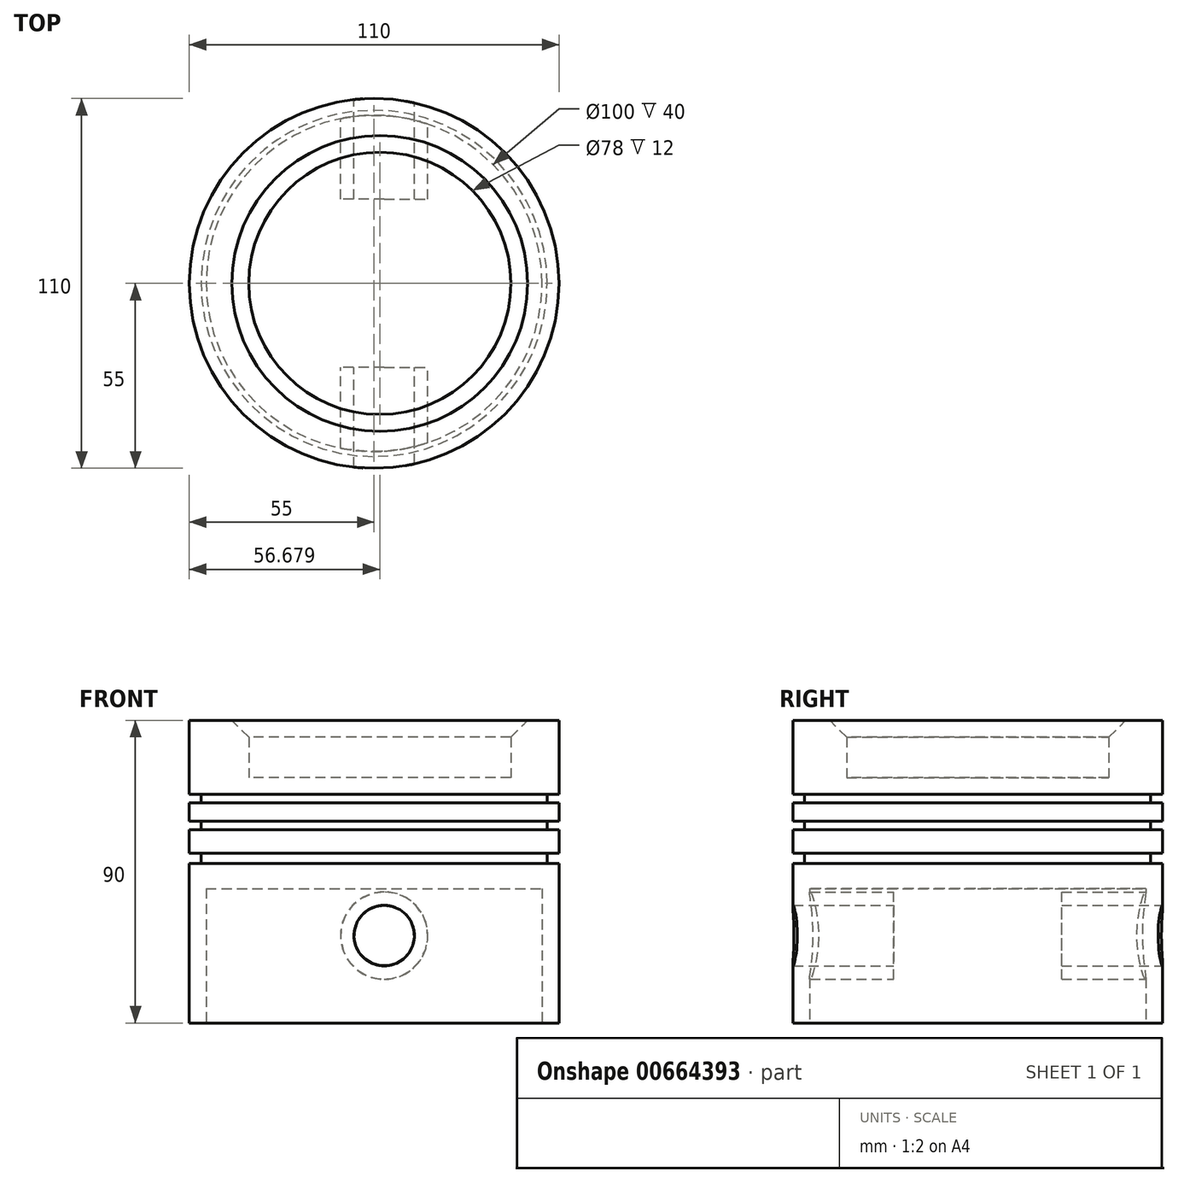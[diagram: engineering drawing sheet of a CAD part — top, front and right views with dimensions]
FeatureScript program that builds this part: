
annotation { "Feature Type Name" : "Feature", "Feature Type Description" : "" }
export const myFeature = defineFeature(function(context is Context, id is Id, definition is map)
    precondition{}
    {
        {
            var Q0;
            Q0=qCreatedBy(makeId("Top.planeOp"),FACE);
            var sketch = newSketch(context, id + "F0", { "sketchPlane" : qUnion([Q0])});
            skCircle(sketch, "E0", {"center": v(0, 0) * mm, "radius": 55 * mm});
            skSolve(sketch);
        }
        {
            var Q0;
            Q0 = qSketchRegion(id + "F0", true);
            extrude(context, id + "F1", {"entities" : qUnion([Q0]), "depth" : 47.5 * mm, "offsetDistance" : 25 * mm});
        }
        {
            var Q0;
            Q0=makeQuery(id+"F1.opExtrude","CAP_FACE",FACE,{"disambiguationData":[OSD([sQuery(id+"F0.wireOp",EDGE,"E0")])],"isStart":false});
            var sketch = newSketch(context, id + "F2", { "sketchPlane" : qUnion([Q0])});
            skCircle(sketch, "E1", {"center": v(0, 0) * mm, "radius": 51.5 * mm});
            skSolve(sketch);
        }
        {
            var Q0;
            Q0 = qSketchRegion(id + "F2", true);
            extrude(context, id + "F3", {"entities" : qUnion([Q0]), "operationType" : NewBodyOperationType.ADD, "depth" : 3 * mm, "offsetDistance" : 25 * mm});
        }
        {
            var Q0;
            Q0=makeQuery(id+"F3.opExtrude","CAP_FACE",FACE,{"disambiguationData":[OSD([sQuery(id+"F2.wireOp",EDGE,"E1")])],"isStart":false});
            var sketch = newSketch(context, id + "F4", { "sketchPlane" : qUnion([Q0])});
            skCircle(sketch, "E2", {"center": v(0, 0) * mm, "radius": 55 * mm});
            skSolve(sketch);
        }
        {
            var Q0;
            Q0 = qSketchRegion(id + "F4", true);
            extrude(context, id + "F5", {"entities" : qUnion([Q0]), "operationType" : NewBodyOperationType.ADD, "depth" : 7 * mm, "offsetDistance" : 25 * mm});
        }
        {
            var Q0;
            Q0=makeQuery(id+"F5.opExtrude","CAP_FACE",FACE,{"disambiguationData":[OSD([sQuery(id+"F4.wireOp",EDGE,"E2")])],"isStart":false});
            var sketch = newSketch(context, id + "F6", { "sketchPlane" : qUnion([Q0])});
            skCircle(sketch, "E3", {"center": v(0, 0) * mm, "radius": 51.5 * mm});
            skSolve(sketch);
        }
        {
            var Q0;
            Q0 = qSketchRegion(id + "F6", true);
            extrude(context, id + "F7", {"entities" : qUnion([Q0]), "operationType" : NewBodyOperationType.ADD, "depth" : 2.5 * mm, "offsetDistance" : 25 * mm});
        }
        {
            var Q0;
            Q0=makeQuery(id+"F7.opExtrude","CAP_FACE",FACE,{"disambiguationData":[OSD([sQuery(id+"F6.wireOp",EDGE,"E3")])],"isStart":false});
            var sketch = newSketch(context, id + "F8", { "sketchPlane" : qUnion([Q0])});
            skCircle(sketch, "E4", {"center": v(0, 0) * mm, "radius": 55 * mm});
            skSolve(sketch);
        }
        {
            var Q0;
            Q0 = qSketchRegion(id + "F8", true);
            extrude(context, id + "F9", {"entities" : qUnion([Q0]), "operationType" : NewBodyOperationType.ADD, "depth" : 5.5 * mm, "offsetDistance" : 25 * mm});
        }
        {
            var Q0;
            Q0=makeQuery(id+"F9.opExtrude","CAP_FACE",FACE,{"disambiguationData":[OSD([sQuery(id+"F8.wireOp",EDGE,"E4")])],"isStart":false});
            var sketch = newSketch(context, id + "F10", { "sketchPlane" : qUnion([Q0])});
            skCircle(sketch, "E5", {"center": v(0, 0) * mm, "radius": 51.5 * mm});
            skSolve(sketch);
        }
        {
            var Q0;
            Q0 = qSketchRegion(id + "F10", true);
            extrude(context, id + "F11", {"entities" : qUnion([Q0]), "operationType" : NewBodyOperationType.ADD, "depth" : 2.5 * mm, "offsetDistance" : 25 * mm});
        }
        {
            var Q0;
            Q0=makeQuery(id+"F11.opExtrude","CAP_FACE",FACE,{"disambiguationData":[OSD([sQuery(id+"F10.wireOp",EDGE,"E5")])],"isStart":false});
            var sketch = newSketch(context, id + "F12", { "sketchPlane" : qUnion([Q0])});
            skCircle(sketch, "E6", {"center": v(0, 0) * mm, "radius": 55 * mm});
            skCircle(sketch, "E7", {"center": v(1.68, 0) * mm, "radius": 39 * mm});
            skSolve(sketch);
        }
        {
            var Q0;
            Q0 = qSketchRegion(id + "F12", true);
            extrude(context, id + "F13", {"entities" : qUnion([Q0]), "operationType" : NewBodyOperationType.ADD, "depth" : 22 * mm, "offsetDistance" : 25 * mm});
        }
        {
            var Q0;
            Q0=makeQuery(id+"F1.opExtrude","CAP_FACE",FACE,{"disambiguationData":[OSD([sQuery(id+"F0.wireOp",EDGE,"E0")])],"isStart":true});
            var sketch = newSketch(context, id + "F14", { "sketchPlane" : qUnion([Q0])});
            skCircle(sketch, "E8", {"center": v(0, 0) * mm, "radius": 50 * mm});
            skSolve(sketch);
        }
        {
            var Q0;
            Q0 = qSketchRegion(id + "F14", true);
            extrude(context, id + "F15", {"entities" : qUnion([Q0]), "operationType" : NewBodyOperationType.REMOVE, "oppositeDirection" : true, "depth" : 40 * mm, "offsetDistance" : 25 * mm});
        }
        {
            var Q0;
            Q0=makeQuery(id+"F11.opExtrude","CAP_FACE",FACE,{"disambiguationData":[OSD([sQuery(id+"F10.wireOp",EDGE,"E5")])],"isStart":false});
            var sketch = newSketch(context, id + "F16", { "sketchPlane" : qUnion([Q0])});
            skCircle(sketch, "E9", {"center": v(0, 0) * mm, "radius": 43.5 * mm});
            skSolve(sketch);
        }
        {
            var Q0;
            Q0 = qSketchRegion(id + "F16", true);
            extrude(context, id + "F17", {"entities" : qUnion([Q0]), "operationType" : NewBodyOperationType.ADD, "depth" : 5 * mm, "offsetDistance" : 25 * mm});
        }
        {
            var Q0;
            Q0=makeQuery(id+"F13.opExtrude","CAP_EDGE",EDGE,{"disambiguationData":[OSD([sQuery(id+"F12.wireOp",EDGE,"E7")])],"isStart":false});
            chamfer(context, id + "F18", {"entities" : qUnion([Q0]), "width" : 5 * mm, "tangentPropagation" : true});
        }
        {
            var Q0;
            Q0=qCreatedBy(makeId("Front.planeOp"),FACE);
            var sketch = newSketch(context, id + "F19", { "sketchPlane" : qUnion([Q0])});
            skLineSegment(sketch, "E10", {"start": v(0, 0) * mm, "end": v(0, 26) * mm, "construction": true});
            skLineSegment(sketch, "E11", {"start": v(0, 26) * mm, "end": v(3, 26) * mm, "construction": true});
            skCircle(sketch, "E12", {"center": v(3, 26) * mm, "radius": 9 * mm});
            skCircle(sketch, "E13", {"center": v(3, 26) * mm, "radius": 13 * mm});
            skSolve(sketch);
        }
        {
            var Q0;
            Q0 = qSketchRegion(id + "F19", true);
            extrude(context, id + "F20", {"entities" : qUnion([Q0]), "operationType" : NewBodyOperationType.ADD, "depth" : 62 * mm, "offsetDistance" : 25 * mm, "hasSecondDirection" : true, "secondDirectionOppositeDirection" : true, "secondDirectionDepth" : 70.1 * mm});
        }
        {
            var Q0;
            Q0=qCreatedBy(makeId("Front.planeOp"),FACE);
            var sketch = newSketch(context, id + "F21", { "sketchPlane" : qUnion([Q0])});
            skLineSegment(sketch, "E14", {"start": v(0, 0) * mm, "end": v(0, 26) * mm, "construction": true});
            skLineSegment(sketch, "E15", {"start": v(0, 26) * mm, "end": v(3, 26) * mm, "construction": true});
            skCircle(sketch, "E16", {"center": v(3, 26) * mm, "radius": 9 * mm});
            skSolve(sketch);
        }
        {
            var Q0;
            Q0 = qSketchRegion(id + "F21", true);
            extrude(context, id + "F22", {"entities" : qUnion([Q0]), "operationType" : NewBodyOperationType.REMOVE, "oppositeDirection" : true, "depth" : 75.8 * mm, "offsetDistance" : 25 * mm, "hasSecondDirection" : true, "secondDirectionOppositeDirection" : false, "secondDirectionDepth" : 99.3 * mm});
        }
        {
            var Q0;
            Q0=qCreatedBy(makeId("Top.planeOp"),FACE);
            var sketch = newSketch(context, id + "F23", { "sketchPlane" : qUnion([Q0])});
            skArc(sketch, "E17", {"start": v(-10, 48.99) * mm, "mid": v(-50, 0) * mm, "end": v(-10, -48.99) * mm});
            skLineSegment(sketch, "E18", {"start": v(0, 0) * mm, "end": v(-10, 0) * mm, "construction": true});
            skLineSegment(sketch, "E19", {"start": v(-10, 0) * mm, "end": v(-10, -25) * mm, "construction": true});
            skLineSegment(sketch, "E20", {"start": v(-10, 0) * mm, "end": v(-10, 25) * mm, "construction": true});
            skLineSegment(sketch, "E21", {"start": v(-10, 25) * mm, "end": v(16, 25) * mm, "construction": true});
            skLineSegment(sketch, "E22", {"start": v(16, 25) * mm, "end": v(16, -25) * mm, "construction": true});
            skLineSegment(sketch, "E23", {"start": v(16, -25) * mm, "end": v(-10, -25) * mm, "construction": true});
            skLineSegment(sketch, "E24", {"start": v(16, -25) * mm, "end": v(16, -47.37) * mm});
            skLineSegment(sketch, "E25", {"start": v(16, -25) * mm, "end": v(-10, -25) * mm});
            skLineSegment(sketch, "E26", {"start": v(-10, -25) * mm, "end": v(-10, -48.99) * mm});
            skLineSegment(sketch, "E27", {"start": v(16, 25) * mm, "end": v(16, 47.37) * mm});
            skLineSegment(sketch, "E28", {"start": v(16, 25) * mm, "end": v(-10, 25) * mm});
            skLineSegment(sketch, "E29", {"start": v(-10, 25) * mm, "end": v(-10, 48.99) * mm});
            skArc(sketch, "E30.trimOffspring", {"start": v(16, -47.37) * mm, "mid": v(50, 0) * mm, "end": v(16, 47.37) * mm});
            skSolve(sketch);
        }
        {
            var Q0;
            Q0 = qSketchRegion(id + "F23", true);
            extrude(context, id + "F24", {"entities" : qUnion([Q0]), "operationType" : NewBodyOperationType.REMOVE, "depth" : 40 * mm, "offsetDistance" : 25 * mm});
        }
        {
            var Q0;
            Q0=makeQuery(id+"F15.boolean.opBoolean","COPY",FACE,{"derivedFrom":makeQuery(id+"F15.opExtrude","CAP_FACE",FACE,{"disambiguationData":[OSD([sQuery(id+"F14.wireOp",EDGE,"E8")])],"isStart":false})});
            var sketch = newSketch(context, id + "F25", { "sketchPlane" : qUnion([Q0])});
            skCircle(sketch, "E31", {"center": v(0, 0) * mm, "radius": 55 * mm});
            skCircle(sketch, "E32", {"center": v(0, -2.17) * mm, "radius": 82.17 * mm});
            skSolve(sketch);
        }
        {
            var Q0;
            Q0 = qSketchRegion(id + "F25", true);
            extrude(context, id + "F26", {"entities" : qUnion([Q0]), "operationType" : NewBodyOperationType.REMOVE, "depth" : 32.2 * mm, "offsetDistance" : 25 * mm});
        }
    });
